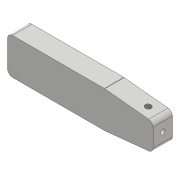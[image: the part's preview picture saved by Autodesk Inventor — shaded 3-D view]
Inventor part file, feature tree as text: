
AUTODESK INVENTOR PART (.ipt)
format: ipt  version: 2018 (Build 220112000, 112)  size: 125,440 bytes
history: native  units: mm
features: sketch x4, extrude x2, hole x2, projected_geometry x2, mirror x1, fillet x1
ambient origin geometry x8: Origin, YZ Plane, XZ Plane, XY Plane, X Axis, Y Axis, Z Axis, Center Point
bodies: Solid1 (feature_tree)
feature tree (12):
  extrude  "Extrusion1"  Depth=60.0mm
  extrude  "Extrusion2"  Depth=20.0mm
  mirror  "Mirror1"
  fillet  "Fillet1"  Radius=2.0mm
  hole  "Hole1"  [1 undecoded]
  hole  "Hole2"  [1 undecoded]
  sketch  "Sketch1"  dims[d0=15.0mm d1=60.0mm]
  sketch  "Sketch2"  dims[d2=8.0mm d3=0.0mm d4=20.0mm d5=2.0mm]
  projected_geometry  "Projected Loop1"
  sketch  "Sketch3"  dims[d6=3.0mm d7=0.0mm d8=2.0mm]
  projected_geometry  "Projected Loop2"
  sketch  "Sketch4"  dims[d9=2.0mm d10=6.0mm d11=4.0mm d12=2.0mm d13=90.0deg d14=8.0mm d15=20.594885mm d16=6.0mm d17=2.459mm d18=10.0mm d19=4.0mm d20=2.0mm d21=90.0deg d22=8.8mm d23=20.594885mm]
note: 2 required parameter values undecoded (feature->parameter linkage not recoverable at this tier; creation-order binding heuristic only, values carry confidence <= 0.55)
